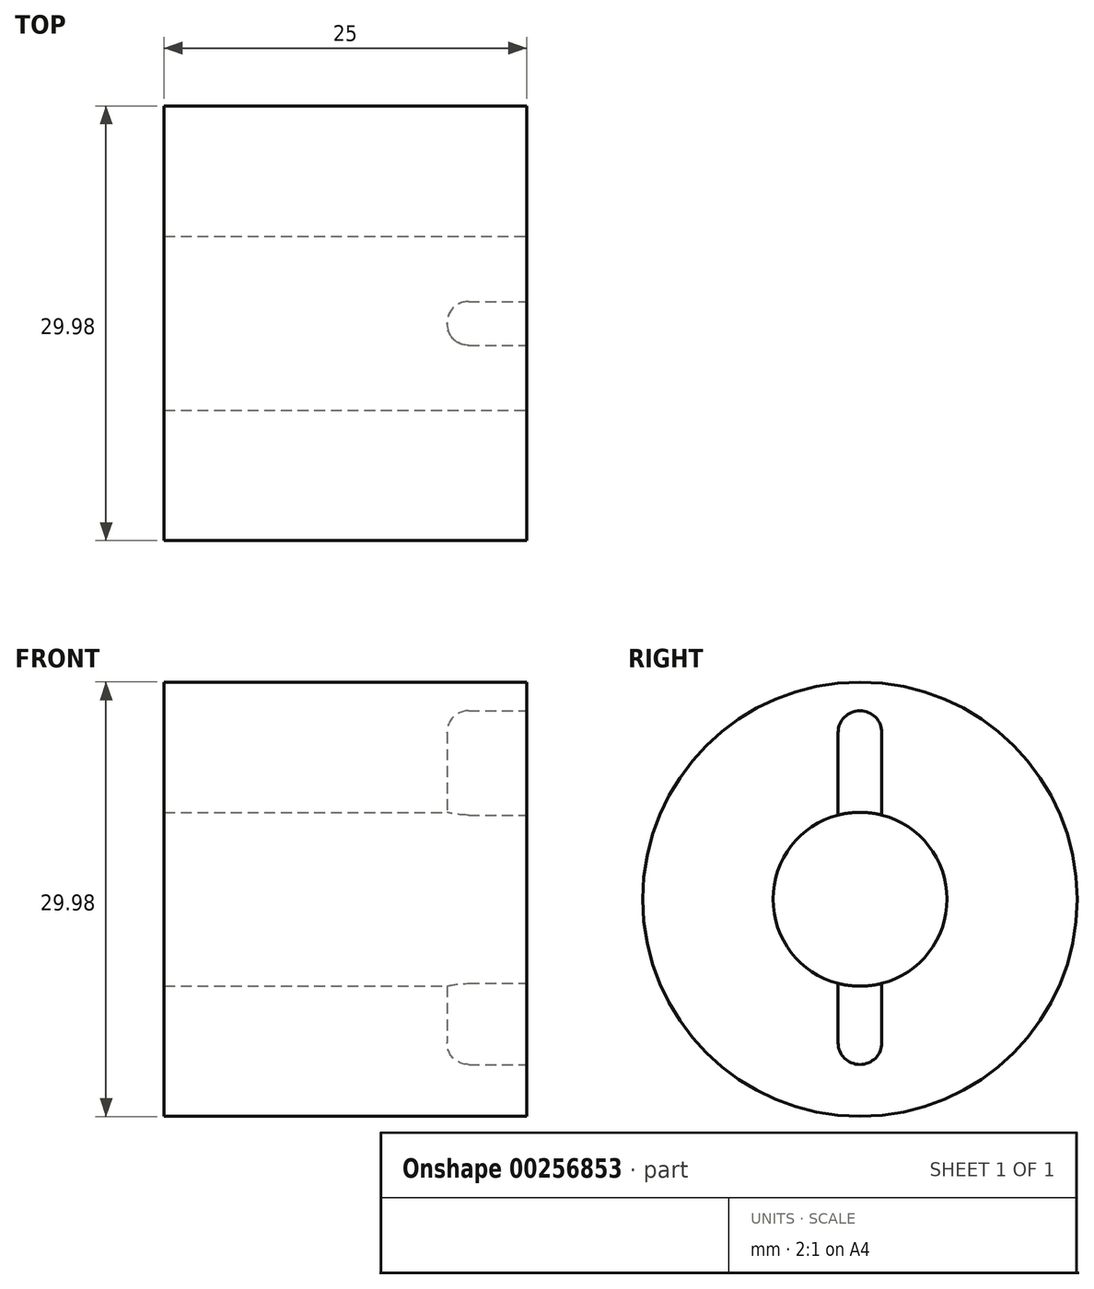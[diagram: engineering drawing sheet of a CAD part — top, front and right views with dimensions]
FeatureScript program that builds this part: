
annotation { "Feature Type Name" : "Feature", "Feature Type Description" : "" }
export const myFeature = defineFeature(function(context is Context, id is Id, definition is map)
    precondition{}
    {
        {
            var Q0;
            Q0=qCreatedBy(makeId("Right.planeOp"),FACE);
            var sketch = newSketch(context, id + "F0", { "sketchPlane" : qUnion([Q0])});
            skCircle(sketch, "E0", {"center": v(0, 0) * mm, "radius": 14.98 * mm});
            skCircle(sketch, "E1", {"center": v(0, 0) * mm, "radius": 6 * mm});
            skSolve(sketch);
        }
        {
            var Q0;
            Q0 = qSketchRegion(id + "F0", true);
            extrude(context, id + "F1", {"entities" : qUnion([Q0]), "oppositeDirection" : true, "depth" : 25 * mm});
        }
        {
            var Q0;
            Q0=qCreatedBy(makeId("Right.planeOp"),FACE);
            var sketch = newSketch(context, id + "F2", { "sketchPlane" : qUnion([Q0])});
            skLineSegment(sketch, "E2", {"start": v(-1.51, 11.5) * mm, "end": v(-1.5, -9.89) * mm});
            skArc(sketch, "E3", {"start": v(-1.5, -9.89) * mm, "mid": v(0, -11.4) * mm, "end": v(1.51, -9.89) * mm});
            skLineSegment(sketch, "E4", {"start": v(1.51, -9.89) * mm, "end": v(1.51, 11.5) * mm});
            skArc(sketch, "E5", {"start": v(1.51, 11.5) * mm, "mid": v(0, 13) * mm, "end": v(-1.51, 11.5) * mm});
            skLineSegment(sketch, "E6", {"start": v(-4.55, 0) * mm, "end": v(4.55, 0) * mm, "construction": true});
            skPoint(sketch, "E7", {"position": v(0, 0) * mm});
            skSolve(sketch);
        }
        {
            var Q0;
            Q0 = qSketchRegion(id + "F2", true);
            extrude(context, id + "F3", {"entities" : qUnion([Q0]), "operationType" : NewBodyOperationType.REMOVE, "oppositeDirection" : true, "depth" : 5.5 * mm});
        }
        {
            var Q0;
            Q0=makeQuery(id+"F3.boolean.opBoolean","COPY",EDGE,{"derivedFrom":makeQuery(id+"F3.opExtrude","CAP_EDGE",EDGE,{"disambiguationData":[OSD([sQuery(id+"F2.wireOp",EDGE,"E4")])],"isStart":false})});
            fillet(context, id + "F4", {"entities" : qUnion([Q0]), "radius" : 1.5 * mm, "tangentPropagation" : true, "allowEdgeOverflow" : false});
        }
    });
